# Revit family: SANINDUSA_110042004_Cetus_Cetus48WallMountedToilet350x490x366_V0
name_source: partatom
category: Plumbing Fixtures
units: mm (PartAtom-declared; Revit-internal decimal feet)

## family parameters
Cut with Voids When Loaded = No
Host = Face
Part Type = Normal
Room Calculation Point = No
Round Connector Dimension = Use Diameter
Shared = No

## types (1)
- SANINDUSA_110042004_Cetus_Cetus48WallMountedToilet350x490x366_V0
    AssetType = Fixed
    CodePerformance = EN 997:2012+A1:2015    CL 1 - 6 A
    Color = white
    Constituents = Compatible toilet seats (not included):21034 - Cetus toilet seat with slowclose system; 21014 - Cetus toilet seat; 453 - Quadro low metal support frame for wall mounted toilet 3/6L; 5E12078 - Plan electronic flush valve powered by transformer with frame for suspended toilet; 5E12077 - Plan electronic flush valve powered by battery with frame for suspended toilet; 449 - Quadro metal support frame for wall mounted toilets with cistern and 3/6L mechanism for plasterboard walls; 443 - Quadro metal support frame for wall mounted toilet with cistern 3/6L;  40533 - Sanbest built-in frame dual flush for wall mounted toilet; 40633 - Sanspace metal support frame for wall mounted toilet with cistern and 3/6L mechanism; 40233 - Sanflush metal support frame for wall mounted toilet with cistern and 3/6L mechanism; 40333 - Sanfix metal support for wall mounted WC with cistern and 3|6L mechanism; 40323 - Sanfix metal support for wall mounted WC with cistern and 3/6L mechanism for plasterboard walls; 41933 - Sanslim pack built-in frame - dual flush and To-Slim plate for wall mounted toilet; 411023 - Sandouble metal support for 2 wall mounted WCs with cistern 3|6Lt for plasterboard walls
    Default Elevation = 1219 mm
    Description = Soil appliance for the disposal of excrement.
    DrainSize = 100 mm  [stored 0.328084 ft]
    Element Type = TOILETPAN: Soil appliance for the disposal of excrement.
    Features = "Domestic and commercial use. Versatile timeless design. Seats easy to clean and slow close option. "
    Finish = gloss
    InletDiameter = 0 mm  [stored 0 ft]
    Installation Instructions = https://www.tec.sanindusa.pt
    Manufacturer = Sanindusa
    ManufacturerName = Sanindusa
    ManufacturerURL = www.tec.sanindusa.pt
    Material = vitreous china
    Model = 110042004
    ModelNumber = 110042004
    ModelReference = Cetus
    Name = Cetus 48 wall mounted toilet
    NominalHeight = 366 mm
    NominalLength = 350 mm  [stored 1.14829 ft]
    NominalWidth = 490 mm  [stored 1.60761 ft]
    PanColor = white
    PanMaterial = vitreous china
    PanMounting = wallhung
    Pre-defined type (IFC) = TOILETPAN
    ProductInformation = https://www.tec.sanindusa.pt
    ProductionYear = 2012
    Size = 350x490x366
    ToiletPanType = washdown
    ToiletType = LooseCoupled
    Type (IFC) = IfcSanitaryTerminalType
    URL = www.tec.sanindusa.pt
    Version = 1
    WarrantyDescription = https://www.tec.sanindusa.pt
    WarrantyDurationParts = 5
    WarrantyDurationUnit = year
    Waste Connection = Yes
    Weight = 13.30 kg

note: [stored X ft] marks values corroborated as IEEE doubles in the binary element streams (Revit-internal decimal feet)

## geometry (parser evidence)
native form markers: Sweep x8
no freeform markers — native parametric forms only
